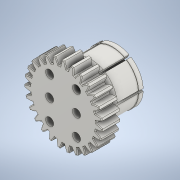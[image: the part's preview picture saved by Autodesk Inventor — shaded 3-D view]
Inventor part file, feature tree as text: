
AUTODESK INVENTOR PART (.ipt)
format: ipt  version: 2022 (Build 260153000, 153)  size: 1,011,200 bytes
history: native  units: mm (DEFAULTED — no unit token found)
features: sketch x9, extrude x7, fillet x5, plane x3, other x3, pattern_circular x3, revolve x1, projected_geometry x1
ambient origin geometry x8: Origin, YZ Plane, XZ Plane, XY Plane, X Axis, Y Axis, Z Axis, Center Point
bodies: Solid1 (feature_tree)
feature tree (32):
  extrude  "Extrusion1"  Depth=6.0mm TaperAngle=0.0deg
  plane  "Work Plane2"
  plane  "Work Plane8"
  plane  "Work Plane9"
  other  "Цилиндрическое зубчатое зацепление"
  extrude  "Выдавливание5"  Depth=10.0mm TaperAngle=0.0deg
  extrude  "Выдавливание7"  Depth=0.4mm
  extrude  "Выдавливание8"  Depth=0.4mm TaperAngle=0.0deg
  revolve  "Вращение1"
  extrude  "Выдавливание9"  TaperAngle=0.0deg  [1 undecoded]
  extrude  "Выдавливание11"  TaperAngle=0.0deg  [1 undecoded]
  fillet  "Сопряжение4"  Radius=40.825mm
  pattern_circular  "Круговой массив2"  [2 undecoded]
  fillet  "Сопряжение5"  [1 undecoded]
  fillet  "Сопряжение6"  Radius=4.0mm
  pattern_circular  "Круговой массив4"  [2 undecoded]
  extrude  "Выдавливание10"  Depth=0.4mm
  fillet  "Сопряжение2"  Radius=4.5mm
  pattern_circular  "Круговой массив1"  Count=3  [1 undecoded]
  fillet  "Сопряжение3"  Radius=8.0mm
  sketch  "Sketch1"  dims[d0=43.480844mm d1=6.0mm d2=0.0mm]
  sketch  "Sketch2"  dims[d3=40.5mm d4=10.0mm d5=0.0mm d16=40.825mm d17=0.0mm d34=1.163553mm d39=0.0mm d41=0.0mm d43=40.825mm d46=40.825mm d47=0.0mm d48=0.0mm d74=4.0mm d75=0.0mm d80=15.0mm d81=23.0mm d82=4.5mm d83=30.0mm d85=11.5mm d86=20.0mm d88=15.0mm d91=8.0mm d92=0.0mm d93=25.4mm d94=2.0mm d95=0.436332mm d96=60.0mm d98=360.0deg d100=20.0mm d101=0.0mm d102=2.5mm d103=0.3mm d104=12.0mm d105=90.0deg d106=21.0mm d107=20.0mm d108=0.0mm d109=0.5mm d110=10.0mm d111=0.0mm d112=1.0mm d113=80.0mm d114=360.0deg d116=0.5mm d117=0.3mm d118=0.872665mm d119=10.0mm d120=0.0mm d121=0.3mm d122=80.0mm d123=360.0deg d125=0.3mm d126=0.4mm d130=270.0mm d131=360.0deg]
  other  "Srf1"
  sketch  "Эскиз6"
  projected_geometry  "Спроецированная петля1"
  sketch  "Эскиз8"
  sketch  "Эскиз9"
  sketch  "Эскиз10"
  sketch  "Эскиз11"
  sketch  "Эскиз12"
  sketch  "Эскиз13"
  other  "Средний диаметр"
note: 8 required parameter values undecoded (feature->parameter linkage not recoverable at this tier; creation-order binding heuristic only, values carry confidence <= 0.55)
